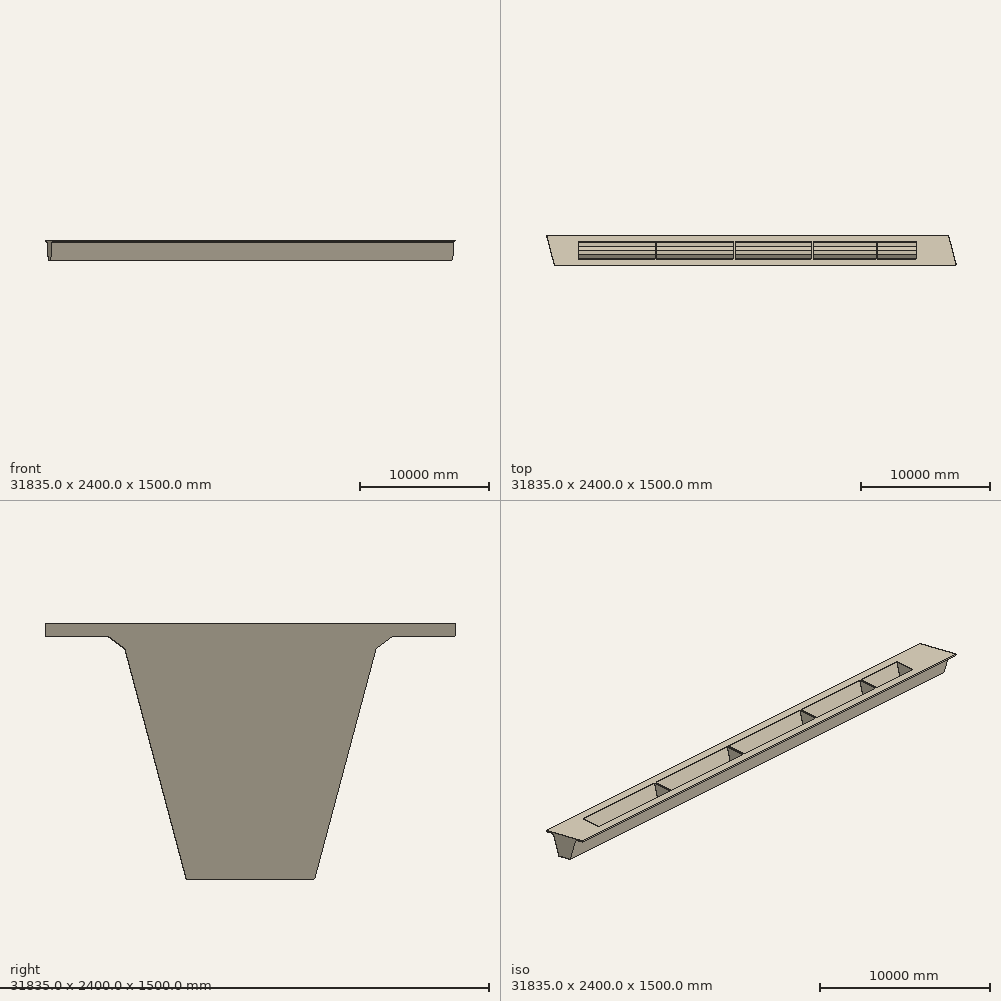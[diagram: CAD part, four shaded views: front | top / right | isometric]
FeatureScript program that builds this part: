
annotation { "Feature Type Name" : "Feature", "Feature Type Description" : "" }
export const myFeature = defineFeature(function(context is Context, id is Id, definition is map)
    precondition{}
    {
        {
            var Q0;
            Q0=qCreatedBy(makeId("Right.planeOp"),FACE);
            var sketch = newSketch(context, id + "F0", { "sketchPlane" : qUnion([Q0])});
            skLineSegment(sketch, "E0", {"start": v(-375.5, 0) * mm, "end": v(-735.36, 1350) * mm});
            skLineSegment(sketch, "E1", {"start": v(-835.36, 1425) * mm, "end": v(-735.36, 1350) * mm});
            skLineSegment(sketch, "E2", {"start": v(-835.36, 1425) * mm, "end": v(-1200, 1425) * mm});
            skLineSegment(sketch, "E3", {"start": v(-1200, 1425) * mm, "end": v(-1200, 1500) * mm});
            skLineSegment(sketch, "E4", {"start": v(0, -1542.66) * mm, "end": v(0, 2021) * mm, "construction": true});
            skLineSegment(sketch, "E5", {"start": v(-375.5, 0) * mm, "end": v(0, 0) * mm});
            skLineSegment(sketch, "E6", {"start": v(-1200, 1500) * mm, "end": v(0, 1500) * mm});
            skLineSegment(sketch, "E7.MirrorCS", {"start": v(1200, 1425) * mm, "end": v(1200, 1500) * mm});
            skLineSegment(sketch, "E8.MirrorCS", {"start": v(835.36, 1425) * mm, "end": v(1200, 1425) * mm});
            skLineSegment(sketch, "E9.MirrorCS", {"start": v(835.36, 1425) * mm, "end": v(735.36, 1350) * mm});
            skLineSegment(sketch, "E10.MirrorCS", {"start": v(1200, 1500) * mm, "end": v(0, 1500) * mm});
            skLineSegment(sketch, "E11.MirrorCS", {"start": v(375.5, 0) * mm, "end": v(735.36, 1350) * mm});
            skLineSegment(sketch, "E12.MirrorCS", {"start": v(375.5, 0) * mm, "end": v(0, 0) * mm});
            skSolve(sketch);
        }
        {
            var Q0;
            Q0 = qSketchRegion(id + "F0", true);
            extrude(context, id + "F1", {"entities" : qUnion([Q0]), "oppositeDirection" : true, "depth" : 31835 * mm, "offsetDistance" : 25 * mm});
        }
        {
            var Q0;
            Q0=makeQuery(id+"F1.opExtrude","SWEPT_FACE",FACE,{"disambiguationData":[OSD([sQuery(id+"F0.wireOp",EDGE,"E6"),sQuery(id+"F0.wireOp",EDGE,"E10.MirrorCS")])]});
            var sketch = newSketch(context, id + "F2", { "sketchPlane" : qUnion([Q0])});
            skLineSegment(sketch, "E13", {"start": v(-31835, 1200) * mm, "end": v(-31205, -1200) * mm});
            skLineSegment(sketch, "E14", {"start": v(-31205, -1200) * mm, "end": v(-31835, -1200) * mm});
            skLineSegment(sketch, "E15", {"start": v(-31835, -1200) * mm, "end": v(-31835, 1200) * mm});
            skLineSegment(sketch, "E16", {"start": v(-31835, 0) * mm, "end": v(-31520, 0) * mm, "construction": true});
            skLineSegment(sketch, "E17", {"start": v(0, -1200) * mm, "end": v(-630, 1200) * mm});
            skLineSegment(sketch, "E18", {"start": v(-630, 1200) * mm, "end": v(0, 1200) * mm});
            skLineSegment(sketch, "E19", {"start": v(0, 1200) * mm, "end": v(0, -1200) * mm});
            skLineSegment(sketch, "E20", {"start": v(0, 0) * mm, "end": v(-315, 0) * mm, "construction": true});
            skSolve(sketch);
        }
        {
            var Q0;
            Q0 = qSketchRegion(id + "F2", true);
            extrude(context, id + "F3", {"entities" : qUnion([Q0]), "operationType" : NewBodyOperationType.REMOVE, "endBound" : BoundingType.THROUGH_ALL, "oppositeDirection" : true, "depth" : 25 * mm, "offsetDistance" : 25 * mm});
        }
        {
            var Q0;
            Q0=qCreatedBy(makeId("Right.planeOp"),FACE);
            cPlane(context, id + "F4", {"entities" : qUnion([Q0]), "cplaneType" : CPlaneType.OFFSET, "offset" : 3130 * mm, "oppositeDirection" : true, "width" : 150 * mm, "height" : 150 * mm});
        }
        {
            var Q0;
            Q0=qCreatedBy(id+"F4.planeOp",FACE);
            var sketch = newSketch(context, id + "F5", { "sketchPlane" : qUnion([Q0])});
            skLineSegment(sketch, "E21", {"start": v(0, 0) * mm, "end": v(0, 1593.87) * mm, "construction": true});
            skLineSegment(sketch, "E22", {"start": v(-667.77, 1475) * mm, "end": v(-667.77, 1500) * mm});
            skLineSegment(sketch, "E23", {"start": v(-667.77, 1500) * mm, "end": v(0, 1500) * mm});
            skLineSegment(sketch, "E24", {"start": v(-667.77, 1475) * mm, "end": v(-642.77, 1475) * mm});
            skLineSegment(sketch, "E25", {"start": v(-642.77, 1475) * mm, "end": v(-308, 257.58) * mm});
            skLineSegment(sketch, "E26", {"start": v(-308, 257.58) * mm, "end": v(0, 199.58) * mm});
            skLineSegment(sketch, "E27.MirrorCS", {"start": v(667.77, 1500) * mm, "end": v(0, 1500) * mm});
            skLineSegment(sketch, "E28.MirrorCS", {"start": v(667.77, 1475) * mm, "end": v(667.77, 1500) * mm});
            skLineSegment(sketch, "E29.MirrorCS", {"start": v(667.77, 1475) * mm, "end": v(642.77, 1475) * mm});
            skLineSegment(sketch, "E30.MirrorCS", {"start": v(642.77, 1475) * mm, "end": v(308, 257.58) * mm});
            skLineSegment(sketch, "E31.MirrorCS", {"start": v(308, 257.58) * mm, "end": v(0, 199.58) * mm});
            skSolve(sketch);
        }
        {
            var Q0;
            Q0 = qSketchRegion(id + "F5", true);
            extrude(context, id + "F6", {"entities" : qUnion([Q0]), "operationType" : NewBodyOperationType.REMOVE, "oppositeDirection" : true, "depth" : 2995 * mm, "offsetDistance" : 25 * mm});
        }
        {
            var Q0;
            Q0=qCreatedBy(makeId("Right.planeOp"),FACE);
            cPlane(context, id + "F7", {"entities" : qUnion([Q0]), "cplaneType" : CPlaneType.OFFSET, "offset" : 6225 * mm, "oppositeDirection" : true, "width" : 150 * mm, "height" : 150 * mm});
        }
        {
            var Q0;
            Q0=qCreatedBy(id+"F7.planeOp",FACE);
            var sketch = newSketch(context, id + "F8", { "sketchPlane" : qUnion([Q0])});
            skLineSegment(sketch, "E32", {"start": v(0, 0) * mm, "end": v(0, 1593.87) * mm, "construction": true});
            skLineSegment(sketch, "E33", {"start": v(-667.77, 1475) * mm, "end": v(-667.77, 1500) * mm});
            skLineSegment(sketch, "E34", {"start": v(-667.77, 1500) * mm, "end": v(0, 1500) * mm});
            skLineSegment(sketch, "E35", {"start": v(-667.77, 1475) * mm, "end": v(-642.77, 1475) * mm});
            skLineSegment(sketch, "E36", {"start": v(-642.77, 1475) * mm, "end": v(-308, 257.58) * mm});
            skLineSegment(sketch, "E37", {"start": v(-308, 257.58) * mm, "end": v(0, 199.58) * mm});
            skLineSegment(sketch, "E38.MirrorCS", {"start": v(667.77, 1500) * mm, "end": v(0, 1500) * mm});
            skLineSegment(sketch, "E39.MirrorCS", {"start": v(667.77, 1475) * mm, "end": v(667.77, 1500) * mm});
            skLineSegment(sketch, "E40.MirrorCS", {"start": v(667.77, 1475) * mm, "end": v(642.77, 1475) * mm});
            skLineSegment(sketch, "E41.MirrorCS", {"start": v(642.77, 1475) * mm, "end": v(308, 257.58) * mm});
            skLineSegment(sketch, "E42.MirrorCS", {"start": v(308, 257.58) * mm, "end": v(0, 199.58) * mm});
            skSolve(sketch);
        }
        {
            var Q0;
            Q0 = qSketchRegion(id + "F8", true);
            extrude(context, id + "F9", {"entities" : qUnion([Q0]), "operationType" : NewBodyOperationType.REMOVE, "oppositeDirection" : true, "depth" : 4900 * mm, "offsetDistance" : 25 * mm});
        }
        {
            var Q0;
            Q0=qCreatedBy(makeId("Right.planeOp"),FACE);
            cPlane(context, id + "F10", {"entities" : qUnion([Q0]), "cplaneType" : CPlaneType.OFFSET, "offset" : 11225 * mm, "oppositeDirection" : true, "width" : 150 * mm, "height" : 150 * mm});
        }
        {
            var Q0;
            Q0=qCreatedBy(id+"F10.planeOp",FACE);
            var sketch = newSketch(context, id + "F11", { "sketchPlane" : qUnion([Q0])});
            skLineSegment(sketch, "E43", {"start": v(0, 0) * mm, "end": v(0, 1593.87) * mm, "construction": true});
            skLineSegment(sketch, "E44", {"start": v(-667.77, 1475) * mm, "end": v(-667.77, 1500) * mm});
            skLineSegment(sketch, "E45", {"start": v(-667.77, 1500) * mm, "end": v(0, 1500) * mm});
            skLineSegment(sketch, "E46", {"start": v(-667.77, 1475) * mm, "end": v(-642.77, 1475) * mm});
            skLineSegment(sketch, "E47", {"start": v(-642.77, 1475) * mm, "end": v(-308, 257.58) * mm});
            skLineSegment(sketch, "E48", {"start": v(-308, 257.58) * mm, "end": v(0, 199.58) * mm});
            skLineSegment(sketch, "E49.MirrorCS", {"start": v(667.77, 1500) * mm, "end": v(0, 1500) * mm});
            skLineSegment(sketch, "E50.MirrorCS", {"start": v(667.77, 1475) * mm, "end": v(667.77, 1500) * mm});
            skLineSegment(sketch, "E51.MirrorCS", {"start": v(667.77, 1475) * mm, "end": v(642.77, 1475) * mm});
            skLineSegment(sketch, "E52.MirrorCS", {"start": v(642.77, 1475) * mm, "end": v(308, 257.58) * mm});
            skLineSegment(sketch, "E53.MirrorCS", {"start": v(308, 257.58) * mm, "end": v(0, 199.58) * mm});
            skSolve(sketch);
        }
        {
            var Q0;
            Q0 = qSketchRegion(id + "F11", true);
            extrude(context, id + "F12", {"entities" : qUnion([Q0]), "operationType" : NewBodyOperationType.REMOVE, "oppositeDirection" : true, "depth" : 5970 * mm, "offsetDistance" : 25 * mm});
        }
        {
            var Q0;
            Q0=qCreatedBy(makeId("Right.planeOp"),FACE);
            cPlane(context, id + "F13", {"entities" : qUnion([Q0]), "cplaneType" : CPlaneType.OFFSET, "offset" : 17295 * mm, "oppositeDirection" : true, "width" : 150 * mm, "height" : 150 * mm});
        }
        {
            var Q0;
            Q0=qCreatedBy(id+"F13.planeOp",FACE);
            var sketch = newSketch(context, id + "F14", { "sketchPlane" : qUnion([Q0])});
            skLineSegment(sketch, "E54", {"start": v(0, 0) * mm, "end": v(0, 1593.87) * mm, "construction": true});
            skLineSegment(sketch, "E55", {"start": v(-667.77, 1475) * mm, "end": v(-667.77, 1500) * mm});
            skLineSegment(sketch, "E56", {"start": v(-667.77, 1500) * mm, "end": v(0, 1500) * mm});
            skLineSegment(sketch, "E57", {"start": v(-667.77, 1475) * mm, "end": v(-642.77, 1475) * mm});
            skLineSegment(sketch, "E58", {"start": v(-642.77, 1475) * mm, "end": v(-308, 257.58) * mm});
            skLineSegment(sketch, "E59", {"start": v(-308, 257.58) * mm, "end": v(0, 199.58) * mm});
            skLineSegment(sketch, "E60.MirrorCS", {"start": v(667.77, 1500) * mm, "end": v(0, 1500) * mm});
            skLineSegment(sketch, "E61.MirrorCS", {"start": v(667.77, 1475) * mm, "end": v(667.77, 1500) * mm});
            skLineSegment(sketch, "E62.MirrorCS", {"start": v(667.77, 1475) * mm, "end": v(642.77, 1475) * mm});
            skLineSegment(sketch, "E63.MirrorCS", {"start": v(642.77, 1475) * mm, "end": v(308, 257.58) * mm});
            skLineSegment(sketch, "E64.MirrorCS", {"start": v(308, 257.58) * mm, "end": v(0, 199.58) * mm});
            skSolve(sketch);
        }
        {
            var Q0;
            Q0 = qSketchRegion(id + "F14", true);
            extrude(context, id + "F15", {"entities" : qUnion([Q0]), "operationType" : NewBodyOperationType.REMOVE, "oppositeDirection" : true, "depth" : 5970 * mm, "offsetDistance" : 25 * mm});
        }
        {
            var Q0;
            Q0=qCreatedBy(makeId("Right.planeOp"),FACE);
            cPlane(context, id + "F16", {"entities" : qUnion([Q0]), "cplaneType" : CPlaneType.OFFSET, "offset" : 23365 * mm, "oppositeDirection" : true, "width" : 150 * mm, "height" : 150 * mm});
        }
        {
            var Q0;
            Q0=qCreatedBy(id+"F16.planeOp",FACE);
            var sketch = newSketch(context, id + "F17", { "sketchPlane" : qUnion([Q0])});
            skLineSegment(sketch, "E65", {"start": v(0, 0) * mm, "end": v(0, 1593.87) * mm, "construction": true});
            skLineSegment(sketch, "E66", {"start": v(-667.77, 1475) * mm, "end": v(-667.77, 1500) * mm});
            skLineSegment(sketch, "E67", {"start": v(-667.77, 1500) * mm, "end": v(0, 1500) * mm});
            skLineSegment(sketch, "E68", {"start": v(-667.77, 1475) * mm, "end": v(-642.77, 1475) * mm});
            skLineSegment(sketch, "E69", {"start": v(-642.77, 1475) * mm, "end": v(-308, 257.58) * mm});
            skLineSegment(sketch, "E70", {"start": v(-308, 257.58) * mm, "end": v(0, 199.58) * mm});
            skLineSegment(sketch, "E71.MirrorCS", {"start": v(667.77, 1500) * mm, "end": v(0, 1500) * mm});
            skLineSegment(sketch, "E72.MirrorCS", {"start": v(667.77, 1475) * mm, "end": v(667.77, 1500) * mm});
            skLineSegment(sketch, "E73.MirrorCS", {"start": v(667.77, 1475) * mm, "end": v(642.77, 1475) * mm});
            skLineSegment(sketch, "E74.MirrorCS", {"start": v(642.77, 1475) * mm, "end": v(308, 257.58) * mm});
            skLineSegment(sketch, "E75.MirrorCS", {"start": v(308, 257.58) * mm, "end": v(0, 199.58) * mm});
            skSolve(sketch);
        }
        {
            var Q0;
            Q0 = qSketchRegion(id + "F17", true);
            extrude(context, id + "F18", {"entities" : qUnion([Q0]), "operationType" : NewBodyOperationType.REMOVE, "oppositeDirection" : true, "depth" : 5970 * mm, "offsetDistance" : 25 * mm});
        }
    });
